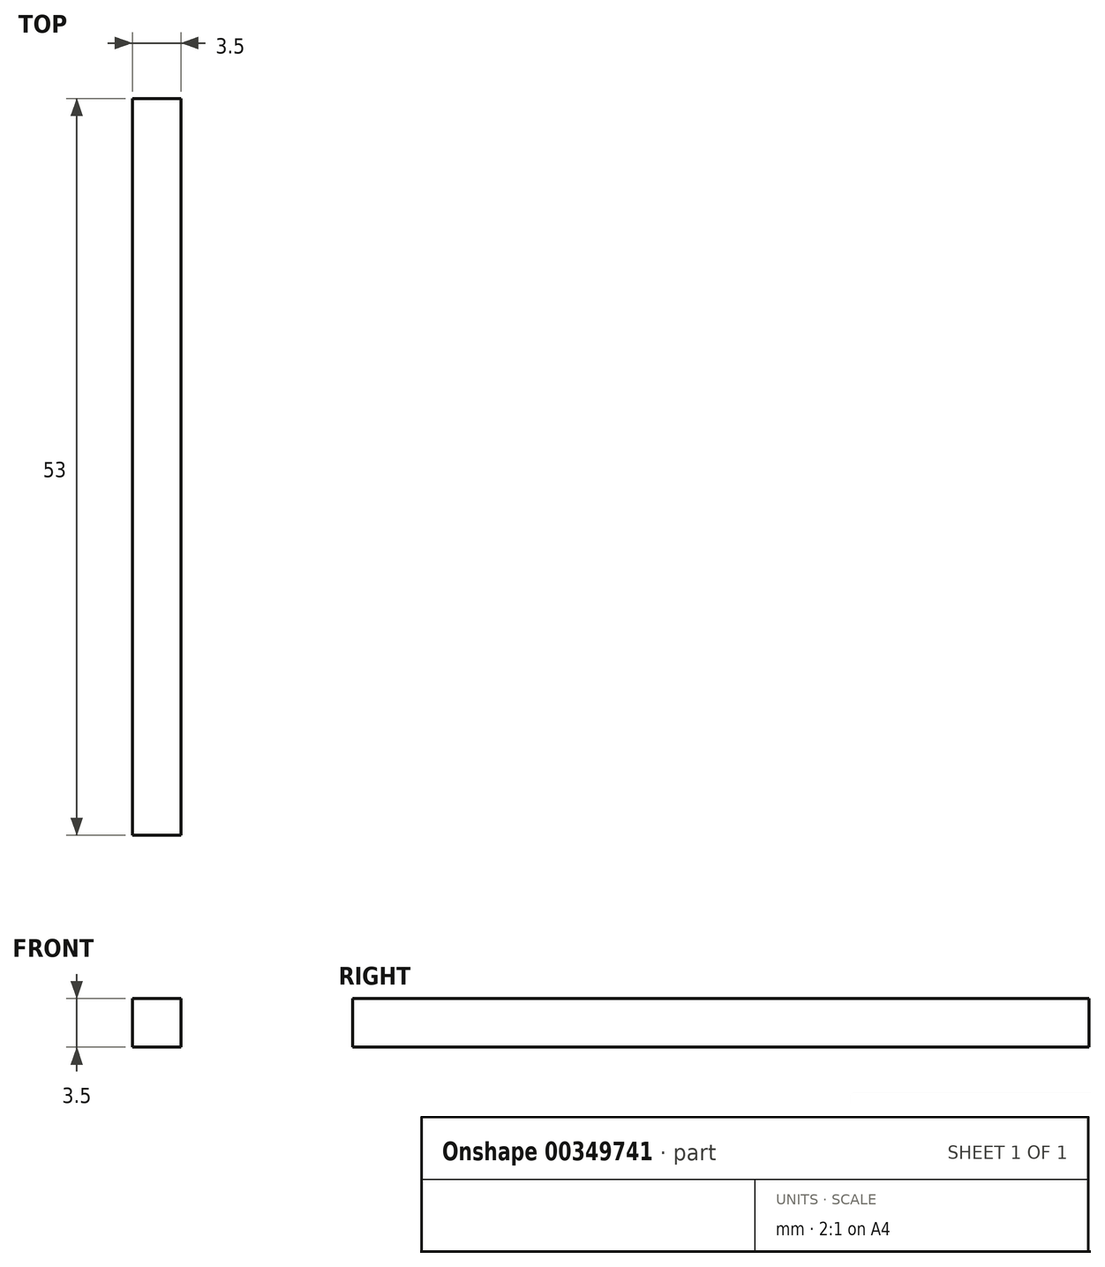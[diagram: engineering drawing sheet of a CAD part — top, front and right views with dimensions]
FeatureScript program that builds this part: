
annotation { "Feature Type Name" : "Feature", "Feature Type Description" : "" }
export const myFeature = defineFeature(function(context is Context, id is Id, definition is map)
    precondition{}
    {
        {
            var Q0;
            Q0=qCreatedBy(makeId("Top.planeOp"),FACE);
            var sketch = newSketch(context, id + "F0", { "sketchPlane" : qUnion([Q0])});
            skLineSegment(sketch, "E0.bottom", {"start": v(1.75, 26.5) * mm, "end": v(-1.75, 26.5) * mm});
            skLineSegment(sketch, "E0.top", {"start": v(1.75, -26.5) * mm, "end": v(-1.75, -26.5) * mm});
            skLineSegment(sketch, "E0.left", {"start": v(1.75, 26.5) * mm, "end": v(1.75, -26.5) * mm});
            skLineSegment(sketch, "E0.right", {"start": v(-1.75, 26.5) * mm, "end": v(-1.75, -26.5) * mm});
            skPoint(sketch, "E0.middle", {"position": v(0, 0) * mm});
            skSolve(sketch);
        }
        {
            var Q0;
            Q0=qSketchRegion(id+"F0",true);
            extrude(context, id + "F1", {"entities" : qUnion([Q0]), "depth" : 3.5 * mm});
        }
    });
